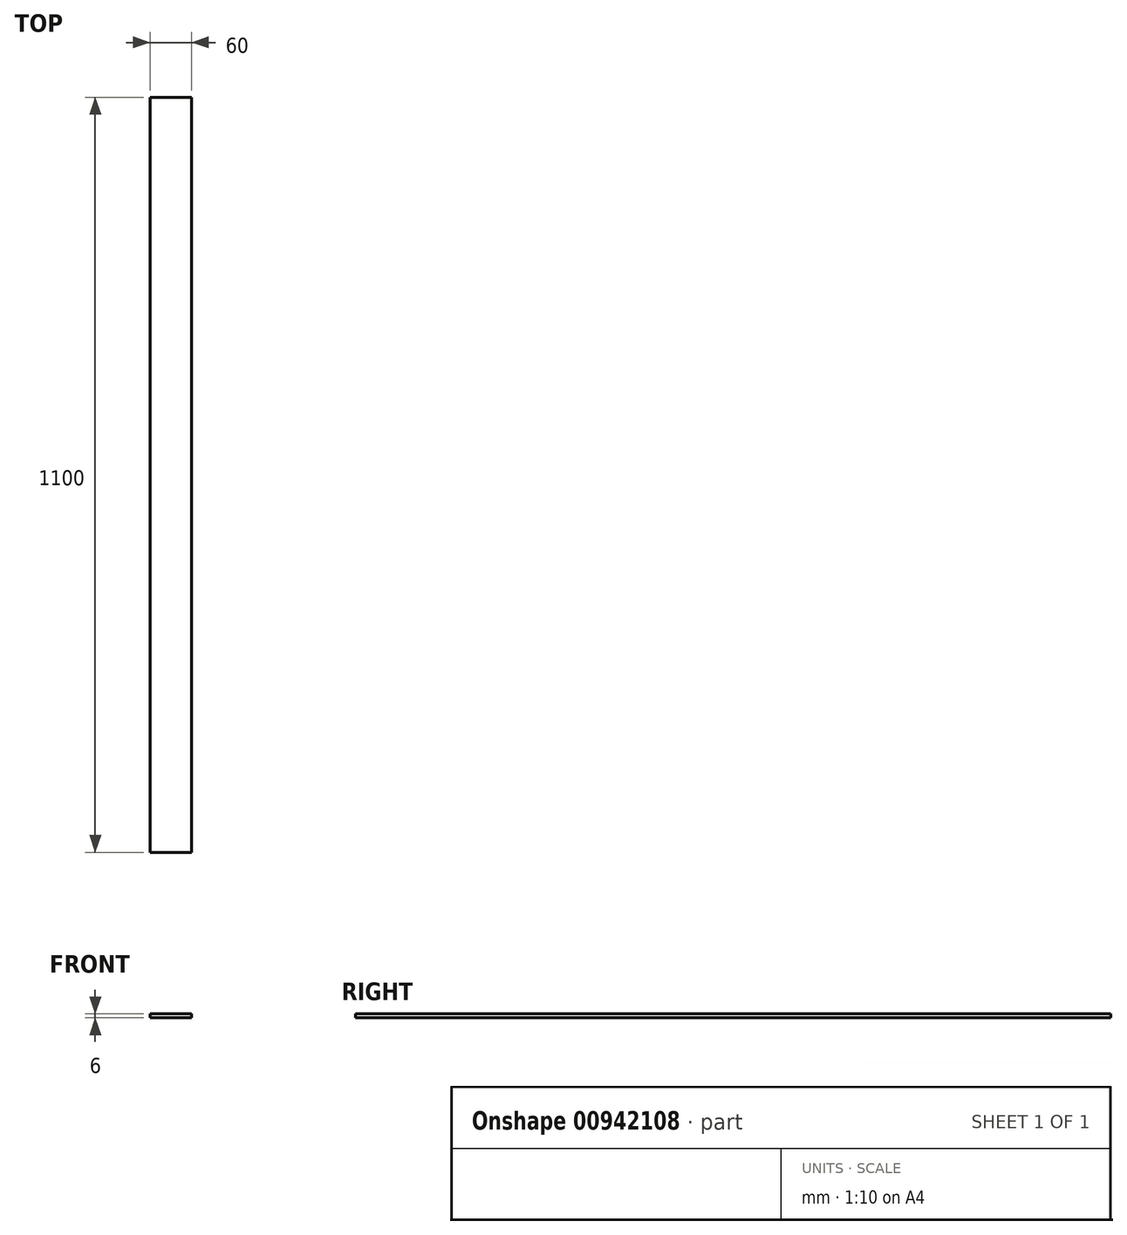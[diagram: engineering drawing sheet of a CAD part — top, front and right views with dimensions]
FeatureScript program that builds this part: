
annotation { "Feature Type Name" : "Feature", "Feature Type Description" : "" }
export const myFeature = defineFeature(function(context is Context, id is Id, definition is map)
    precondition{}
    {
        {
            var Q0;
            Q0=qCreatedBy(makeId("Top.planeOp"),FACE);
            var sketch = newSketch(context, id + "F0", { "sketchPlane" : qUnion([Q0])});
            skLineSegment(sketch, "E0.bottom", {"start": v(0, 0) * mm, "end": v(60, 0) * mm});
            skLineSegment(sketch, "E0.top", {"start": v(0, -1100) * mm, "end": v(60, -1100) * mm});
            skLineSegment(sketch, "E0.left", {"start": v(0, 0) * mm, "end": v(0, -1100) * mm});
            skLineSegment(sketch, "E0.right", {"start": v(60, 0) * mm, "end": v(60, -1100) * mm});
            skSolve(sketch);
        }
        {
            var Q0;
            Q0 = qSketchRegion(id + "F0", true);
            extrude(context, id + "F1", {"entities" : qUnion([Q0]), "depth" : 6 * mm, "offsetDistance" : 25 * mm});
        }
    });
